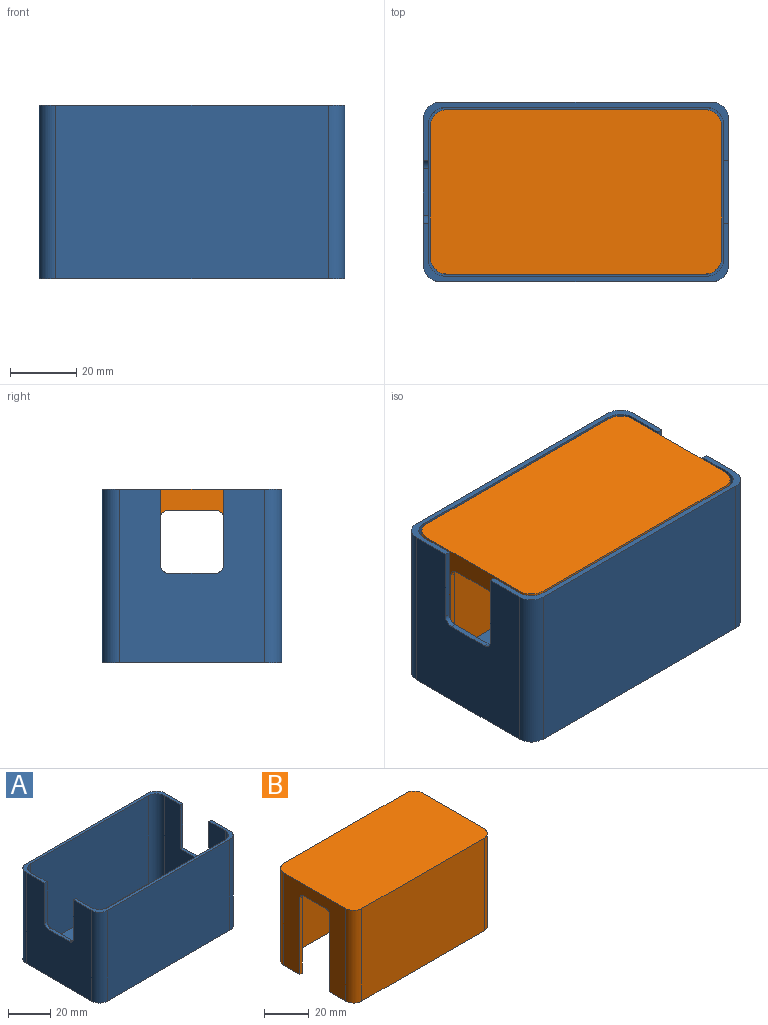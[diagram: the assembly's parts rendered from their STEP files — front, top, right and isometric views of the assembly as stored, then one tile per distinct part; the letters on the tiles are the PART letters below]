
ASSEMBLY  parts=2 mates=1
PART A: 28 faces, bbox 92.1x54x52.4 mm
  f0: plane 92.08x17.46mm, normal (0,0,1), area 196.6mm2, adj f2,f3,f5,f7,f8,f10,f13,f15
  f1: plane 92.08x17.46mm, normal (0,0,1), area 196.6mm2, adj f2,f3,f5,f6,f9,f10,f12,f16
  f2: plane 52.39x43.82mm, normal (1,0,0), area 1811.5mm2, adj f0,f1,f4,f15,f16,f17,f18,f19
  f3: plane 50.8x40.64mm, normal (1,0,0), area 1583.4mm2, adj f0,f1,f11,f12,f13,f14,f24,f25
  f4: plane 92.08x53.98mm, normal (0,0,-1), area 4947.6mm2, adj f2,f8,f9,f10,f18,f19,f20,f21
  f5: plane 50.8x40.64mm, normal (-1,0,0), area 1580.6mm2, adj f0,f1,f11,f15,f16,f17,f22,f23
  f6: plane 78.74x50.8mm, normal (0,-1,0), area 4000mm2, adj f1,f11,f22,f25
  f7: plane 78.74x50.8mm, normal (0,1,0), area 4000mm2, adj f0,f11,f23,f24
  f8: plane 81.92x52.39mm, normal (0,-1,0), area 4291.3mm2, adj f0,f4,f18,f21
  f9: plane 81.92x52.39mm, normal (0,1,0), area 4291.3mm2, adj f1,f4,f19,f20
  f10: plane 52.39x43.82mm, normal (-1,0,0), area 1814.3mm2, adj f0,f1,f4,f12,f13,f14,f20,f21
  f11: plane 88.9x50.8mm, normal (0,0,1), area 4494mm2, adj f3,f5,f6,f7,f22,f23,f24,f25
  f12: plane 22.86x1.59mm, normal (0,-1,0), area 36.3mm2, adj f1,f3,f10,f26
  f13: plane 22.86x1.59mm, normal (0,1,0), area 36.3mm2, adj f0,f3,f10,f27
  f14: plane 13.97x1.59mm, normal (0,0,1), area 22.2mm2, adj f3,f10,f26,f27
  f15: plane 25.4x1.59mm, normal (0,1,0), area 40.3mm2, adj f0,f2,f5,f17
  f16: plane 25.4x1.59mm, normal (0,-1,0), area 40.3mm2, adj f1,f2,f5,f17
  f17: plane 19.05x1.59mm, normal (0,0,1), area 30.2mm2, adj f2,f5,f15,f16
  f18: cylinder r=5.08mm len=52.39mm, axis (0,0,-1), area 418mm2, adj f0,f2,f4,f8
  f19: cylinder r=5.08mm len=52.39mm, axis (0,0,1), area 418mm2, adj f1,f2,f4,f9
  f20: cylinder r=5.08mm len=52.39mm, axis (0,0,-1), area 418mm2, adj f1,f4,f9,f10
  f21: cylinder r=5.08mm len=52.39mm, axis (0,0,1), area 418mm2, adj f0,f4,f8,f10
  f22: cylinder r=5.08mm len=50.8mm, axis (0,0,-1), area 405.4mm2, adj f1,f5,f6,f11
  f23: cylinder r=5.08mm len=50.8mm, axis (0,0,1), area 405.4mm2, adj f0,f5,f7,f11
  f24: cylinder r=5.08mm len=50.8mm, axis (0,0,-1), area 405.4mm2, adj f0,f3,f7,f11
  f25: cylinder r=5.08mm len=50.8mm, axis (0,0,1), area 405.4mm2, adj f1,f3,f6,f11
  f26: cylinder r=2.54mm len=2.54mm, axis (-1,0,0), area 6.3mm2, adj f3,f10,f12,f14
  f27: cylinder r=2.54mm len=2.54mm, axis (1,0,0), area 6.3mm2, adj f3,f10,f13,f14
PART B: 28 faces, bbox 87.6x49.5x50.8 mm
  f0: plane 87.63x15.24mm, normal (0,0,-1), area 182.5mm2, adj f1,f2,f4,f6,f7,f8,f12,f15
  f1: plane 49.21x36.2mm, normal (1,0,0), area 937.2mm2, adj f0,f10,f11,f12,f13,f14,f22,f25
  f2: plane 50.8x39.37mm, normal (1,0,0), area 1153.2mm2, adj f0,f3,f10,f15,f16,f17,f18,f21
  f3: plane 87.63x49.53mm, normal (0,0,1), area 4318.2mm2, adj f2,f7,f8,f9,f18,f19,f20,f21
  f4: plane 74.3x49.21mm, normal (0,-1,0), area 3656.2mm2, adj f0,f11,f22,f23
  f5: plane 74.3x49.21mm, normal (0,1,0), area 3656.2mm2, adj f10,f11,f24,f25
  f6: plane 49.21x36.2mm, normal (-1,0,0), area 934.5mm2, adj f0,f10,f11,f15,f16,f17,f23,f24
  f7: plane 77.47x50.8mm, normal (0,1,0), area 3935.5mm2, adj f0,f3,f18,f19
  f8: plane 50.8x39.37mm, normal (-1,0,0), area 1156mm2, adj f0,f3,f10,f12,f13,f14,f19,f20
  f9: plane 77.47x50.8mm, normal (0,-1,0), area 3935.5mm2, adj f3,f10,f20,f21
  f10: plane 87.63x15.24mm, normal (0,0,-1), area 182.5mm2, adj f1,f2,f5,f6,f8,f9,f13,f16
  f11: plane 84.46x46.36mm, normal (0,0,-1), area 3892.8mm2, adj f1,f4,f5,f6,f22,f23,f24,f25
  f12: plane 41.91x1.59mm, normal (0,-1,0), area 66.5mm2, adj f0,f1,f8,f26
  f13: plane 41.91x1.59mm, normal (0,1,0), area 66.5mm2, adj f1,f8,f10,f27
  f14: plane 13.97x1.59mm, normal (0,0,-1), area 22.2mm2, adj f1,f8,f26,f27
  f15: plane 44.45x1.59mm, normal (0,-1,0), area 70.6mm2, adj f0,f2,f6,f17
  f16: plane 44.45x1.59mm, normal (0,1,0), area 70.6mm2, adj f2,f6,f10,f17
  f17: plane 19.05x1.59mm, normal (0,0,-1), area 30.2mm2, adj f2,f6,f15,f16
  f18: cylinder r=5.08mm len=50.8mm, axis (0,0,-1), area 405.4mm2, adj f0,f2,f3,f7
  f19: cylinder r=5.08mm len=50.8mm, axis (0,0,1), area 405.4mm2, adj f0,f3,f7,f8
  f20: cylinder r=5.08mm len=50.8mm, axis (0,0,-1), area 405.4mm2, adj f3,f8,f9,f10
  f21: cylinder r=5.08mm len=50.8mm, axis (0,0,1), area 405.4mm2, adj f2,f3,f9,f10
  f22: cylinder r=5.08mm len=49.21mm, axis (0,0,-1), area 392.7mm2, adj f0,f1,f4,f11
  f23: cylinder r=5.08mm len=49.21mm, axis (0,0,1), area 392.7mm2, adj f0,f4,f6,f11
  f24: cylinder r=5.08mm len=49.21mm, axis (0,0,-1), area 392.7mm2, adj f5,f6,f10,f11
  f25: cylinder r=5.08mm len=49.21mm, axis (0,0,1), area 392.7mm2, adj f1,f5,f10,f11
  f26: cylinder r=2.54mm len=2.54mm, axis (-1,0,0), area 6.3mm2, adj f1,f8,f12,f14
  f27: cylinder r=2.54mm len=2.54mm, axis (1,0,0), area 6.3mm2, adj f1,f8,f13,f14
PLACE A t=(-25.67,95.44,-19.16)mm
PLACE B t=(-228.23,96.07,33.23)mm
MATE pin_slot A.f11 <-> B.f10  axis (0,0,1) through (-25.67,95.44,-17.57)mm
